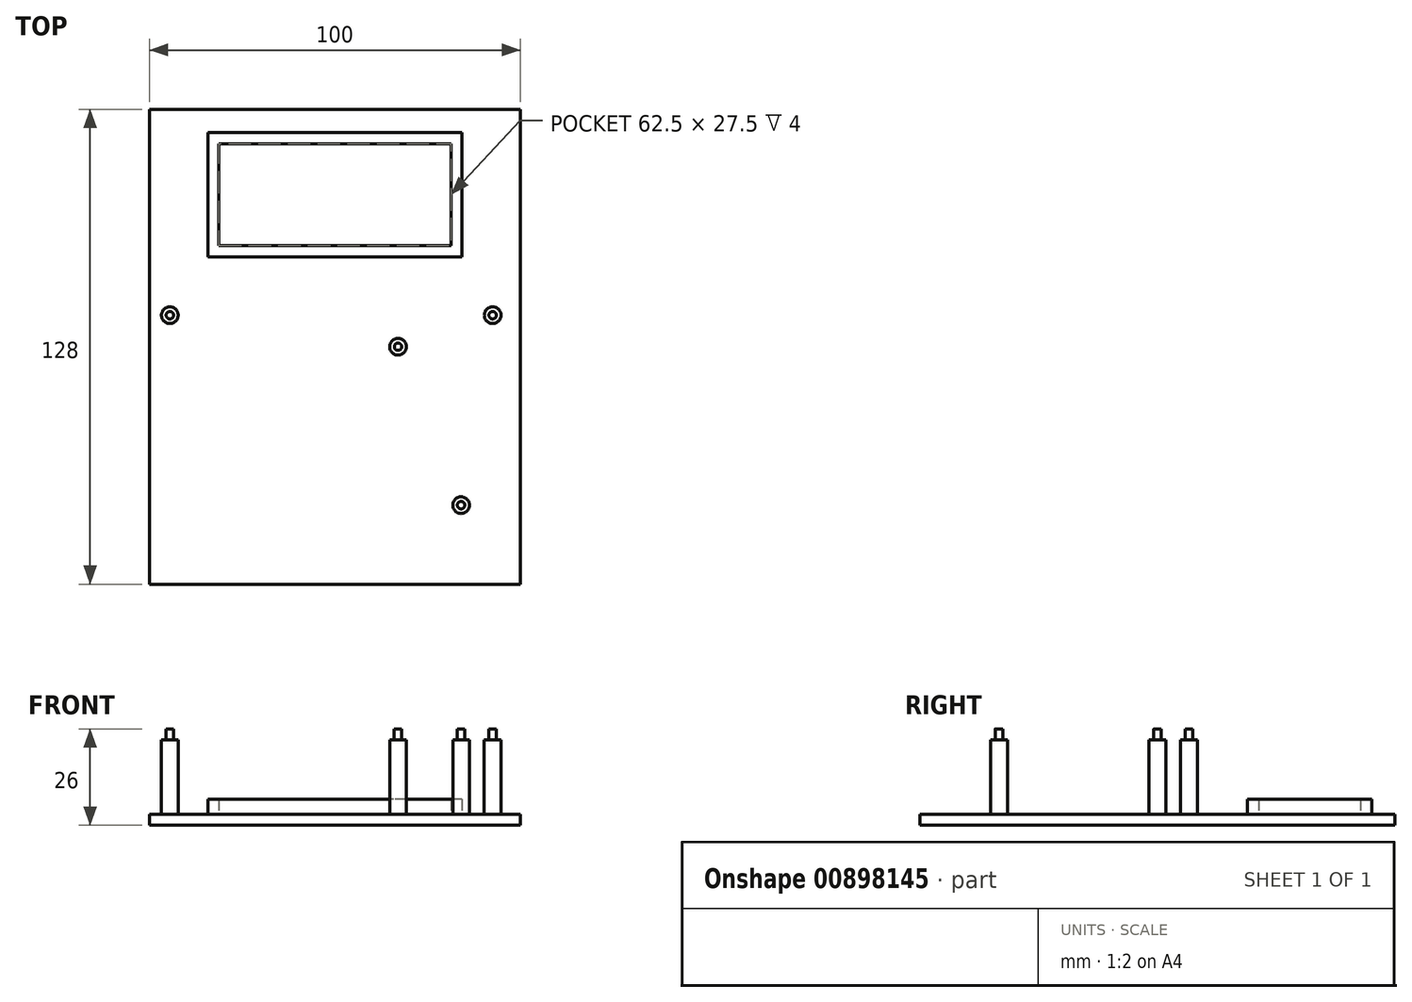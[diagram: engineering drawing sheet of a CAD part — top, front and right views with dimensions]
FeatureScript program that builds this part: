
annotation { "Feature Type Name" : "Feature", "Feature Type Description" : "" }
export const myFeature = defineFeature(function(context is Context, id is Id, definition is map)
    precondition{}
    {
        {
            var Q0;
            Q0=qCreatedBy(makeId("Top.planeOp"),FACE);
            var sketch = newSketch(context, id + "F0", { "sketchPlane" : qUnion([Q0])});
            skLineSegment(sketch, "E0.bottom", {"start": v(50, -60) * mm, "end": v(-50, -60) * mm});
            skLineSegment(sketch, "E0.left", {"start": v(50, -60) * mm, "end": v(50, 68) * mm});
            skLineSegment(sketch, "E0.right", {"start": v(-50, -60) * mm, "end": v(-50, 68) * mm});
            skPoint(sketch, "E0.middle", {"position": v(0, 0) * mm});
            skLineSegment(sketch, "E1", {"start": v(-50, 68) * mm, "end": v(50, 68) * mm});
            skPoint(sketch, "E2.orphan", {"position": v(-50, 60) * mm});
            skPoint(sketch, "E3.orphan", {"position": v(50, 60) * mm});
            skLineSegment(sketch, "E4", {"start": v(-50, 4) * mm, "end": v(50, 4) * mm, "construction": true});
            skLineSegment(sketch, "E5", {"start": v(-50, 12.5) * mm, "end": v(50, 12.5) * mm, "construction": true});
            skLineSegment(sketch, "E6", {"start": v(-50, 21.2) * mm, "end": v(50, 21.2) * mm, "construction": true});
            skCircle(sketch, "E7", {"center": v(-44.5, 12.5) * mm, "radius": 2.25 * mm});
            skCircle(sketch, "E8", {"center": v(42.5, 12.5) * mm, "radius": 2.25 * mm});
            skCircle(sketch, "E9", {"center": v(17, 4) * mm, "radius": 2.25 * mm});
            skCircle(sketch, "E10", {"center": v(34, -38.7) * mm, "radius": 2.25 * mm});
            skLineSegment(sketch, "E11.bottom", {"start": v(31.25, 31.25) * mm, "end": v(-31.25, 31.25) * mm});
            skLineSegment(sketch, "E11.top", {"start": v(31.25, 58.75) * mm, "end": v(-31.25, 58.75) * mm});
            skLineSegment(sketch, "E11.left", {"start": v(31.25, 31.25) * mm, "end": v(31.25, 58.75) * mm});
            skLineSegment(sketch, "E11.right", {"start": v(-31.25, 31.25) * mm, "end": v(-31.25, 58.75) * mm});
            skPoint(sketch, "E11.middle", {"position": v(0, 45) * mm});
            skLineSegment(sketch, "E12.0", {"start": v(34.25, 28.25) * mm, "end": v(34.25, 61.75) * mm});
            skLineSegment(sketch, "E12.1", {"start": v(34.25, 28.25) * mm, "end": v(-34.25, 28.25) * mm});
            skLineSegment(sketch, "E12.2", {"start": v(-34.25, 28.25) * mm, "end": v(-34.25, 61.75) * mm});
            skLineSegment(sketch, "E12.3", {"start": v(34.25, 61.75) * mm, "end": v(-34.25, 61.75) * mm});
            skSolve(sketch);
        }
        {
            var Q0;
            Q0=makeQuery(id+"F0.imprint","IMPRINT",FACE,{"disambiguationData":[TD([[makeQuery(id+"F0.imprint","IMPRINT",EDGE,{"derivedFrom":sQuery(id+"F0.wireOp",EDGE,"E0.bottom")}),-1.0]])]});
            var Q1;
            Q1=makeQuery(id+"F0.imprint","IMPRINT",FACE,{"disambiguationData":[TD([[makeQuery(id+"F0.imprint","IMPRINT",EDGE,{"derivedFrom":sQuery(id+"F0.wireOp",EDGE,"E11.bottom")}),1.0]])]});
            var Q2;
            Q2=makeQuery(id+"F0.imprint","IMPRINT",FACE,{"disambiguationData":[TD([[makeQuery(id+"F0.imprint","IMPRINT",EDGE,{"derivedFrom":sQuery(id+"F0.wireOp",EDGE,"E7")}),1.0]])]});
            var Q3;
            Q3=makeQuery(id+"F0.imprint","IMPRINT",FACE,{"disambiguationData":[TD([[makeQuery(id+"F0.imprint","IMPRINT",EDGE,{"derivedFrom":sQuery(id+"F0.wireOp",EDGE,"E9")}),1.0]])]});
            var Q4;
            Q4=makeQuery(id+"F0.imprint","IMPRINT",FACE,{"disambiguationData":[TD([[makeQuery(id+"F0.imprint","IMPRINT",EDGE,{"derivedFrom":sQuery(id+"F0.wireOp",EDGE,"E8")}),1.0]])]});
            var Q5;
            Q5=makeQuery(id+"F0.imprint","IMPRINT",FACE,{"disambiguationData":[TD([[makeQuery(id+"F0.imprint","IMPRINT",EDGE,{"derivedFrom":sQuery(id+"F0.wireOp",EDGE,"E11.bottom")}),-1.0]])]});
            var Q6;
            Q6=makeQuery(id+"F0.imprint","IMPRINT",FACE,{"disambiguationData":[TD([[makeQuery(id+"F0.imprint","IMPRINT",EDGE,{"derivedFrom":sQuery(id+"F0.wireOp",EDGE,"E10")}),1.0]])]});
            extrude(context, id + "F1", {"entities" : qUnion([Q0, Q1, Q2, Q3, Q4, Q5, Q6]), "depth" : -3 * mm, "offsetDistance" : 25 * mm});
        }
        {
            var Q0;
            Q0=makeQuery(id+"F0.imprint","IMPRINT",FACE,{"disambiguationData":[TD([[makeQuery(id+"F0.imprint","IMPRINT",EDGE,{"derivedFrom":sQuery(id+"F0.wireOp",EDGE,"E7")}),1.0]])]});
            var Q1;
            Q1=makeQuery(id+"F0.imprint","IMPRINT",FACE,{"disambiguationData":[TD([[makeQuery(id+"F0.imprint","IMPRINT",EDGE,{"derivedFrom":sQuery(id+"F0.wireOp",EDGE,"E9")}),1.0]])]});
            var Q2;
            Q2=makeQuery(id+"F0.imprint","IMPRINT",FACE,{"disambiguationData":[TD([[makeQuery(id+"F0.imprint","IMPRINT",EDGE,{"derivedFrom":sQuery(id+"F0.wireOp",EDGE,"E8")}),1.0]])]});
            var Q3;
            Q3=makeQuery(id+"F0.imprint","IMPRINT",FACE,{"disambiguationData":[TD([[makeQuery(id+"F0.imprint","IMPRINT",EDGE,{"derivedFrom":sQuery(id+"F0.wireOp",EDGE,"E10")}),1.0]])]});
            extrude(context, id + "F2", {"entities" : qUnion([Q0, Q1, Q2, Q3]), "operationType" : NewBodyOperationType.ADD, "depth" : 20 * mm, "offsetDistance" : 25 * mm});
        }
        {
            var Q0;
            Q0=makeQuery(id+"F0.imprint","IMPRINT",FACE,{"disambiguationData":[TD([[makeQuery(id+"F0.imprint","IMPRINT",EDGE,{"derivedFrom":sQuery(id+"F0.wireOp",EDGE,"E11.bottom")}),1.0]])]});
            extrude(context, id + "F3", {"entities" : qUnion([Q0]), "operationType" : NewBodyOperationType.ADD, "depth" : 4 * mm, "offsetDistance" : 25 * mm});
        }
        {
            var Q0;
            Q0=makeQuery(id+"F2.opExtrude","CAP_FACE",FACE,{"disambiguationData":[OSD([sQuery(id+"F0.wireOp",EDGE,"E7")])],"isStart":false});
            var sketch = newSketch(context, id + "F4", { "sketchPlane" : qUnion([Q0])});
            skCircle(sketch, "E13", {"center": v(-44.5, 12.5) * mm, "radius": 1 * mm});
            skSolve(sketch);
        }
        {
            var Q0;
            Q0 = qSketchRegion(id + "F4", true);
            extrude(context, id + "F5", {"entities" : qUnion([Q0]), "operationType" : NewBodyOperationType.ADD, "depth" : 3 * mm, "offsetDistance" : 25 * mm});
        }
        {
            var Q0;
            Q0=makeQuery(id+"F2.opExtrude","CAP_FACE",FACE,{"disambiguationData":[OSD([sQuery(id+"F0.wireOp",EDGE,"E9")])],"isStart":false});
            var sketch = newSketch(context, id + "F6", { "sketchPlane" : qUnion([Q0])});
            skCircle(sketch, "E14", {"center": v(17, 4) * mm, "radius": 1 * mm});
            skSolve(sketch);
        }
        {
            var Q0;
            Q0 = qSketchRegion(id + "F6", true);
            extrude(context, id + "F7", {"entities" : qUnion([Q0]), "operationType" : NewBodyOperationType.ADD, "depth" : 3 * mm, "offsetDistance" : 25 * mm});
        }
        {
            var Q0;
            Q0=makeQuery(id+"F2.opExtrude","CAP_FACE",FACE,{"disambiguationData":[OSD([sQuery(id+"F0.wireOp",EDGE,"E8")])],"isStart":false});
            var sketch = newSketch(context, id + "F8", { "sketchPlane" : qUnion([Q0])});
            skCircle(sketch, "E15", {"center": v(42.5, 12.5) * mm, "radius": 1 * mm});
            skSolve(sketch);
        }
        {
            var Q0;
            Q0 = qSketchRegion(id + "F8", true);
            extrude(context, id + "F9", {"entities" : qUnion([Q0]), "operationType" : NewBodyOperationType.ADD, "depth" : 3 * mm, "offsetDistance" : 25 * mm});
        }
        {
            var Q0;
            Q0=makeQuery(id+"F2.opExtrude","CAP_FACE",FACE,{"disambiguationData":[OSD([sQuery(id+"F0.wireOp",EDGE,"E10")])],"isStart":false});
            var sketch = newSketch(context, id + "F10", { "sketchPlane" : qUnion([Q0])});
            skCircle(sketch, "E16", {"center": v(34, -38.7) * mm, "radius": 1 * mm});
            skSolve(sketch);
        }
        {
            var Q0;
            Q0 = qSketchRegion(id + "F10", true);
            extrude(context, id + "F11", {"entities" : qUnion([Q0]), "operationType" : NewBodyOperationType.ADD, "depth" : 3 * mm, "offsetDistance" : 25 * mm});
        }
    });
